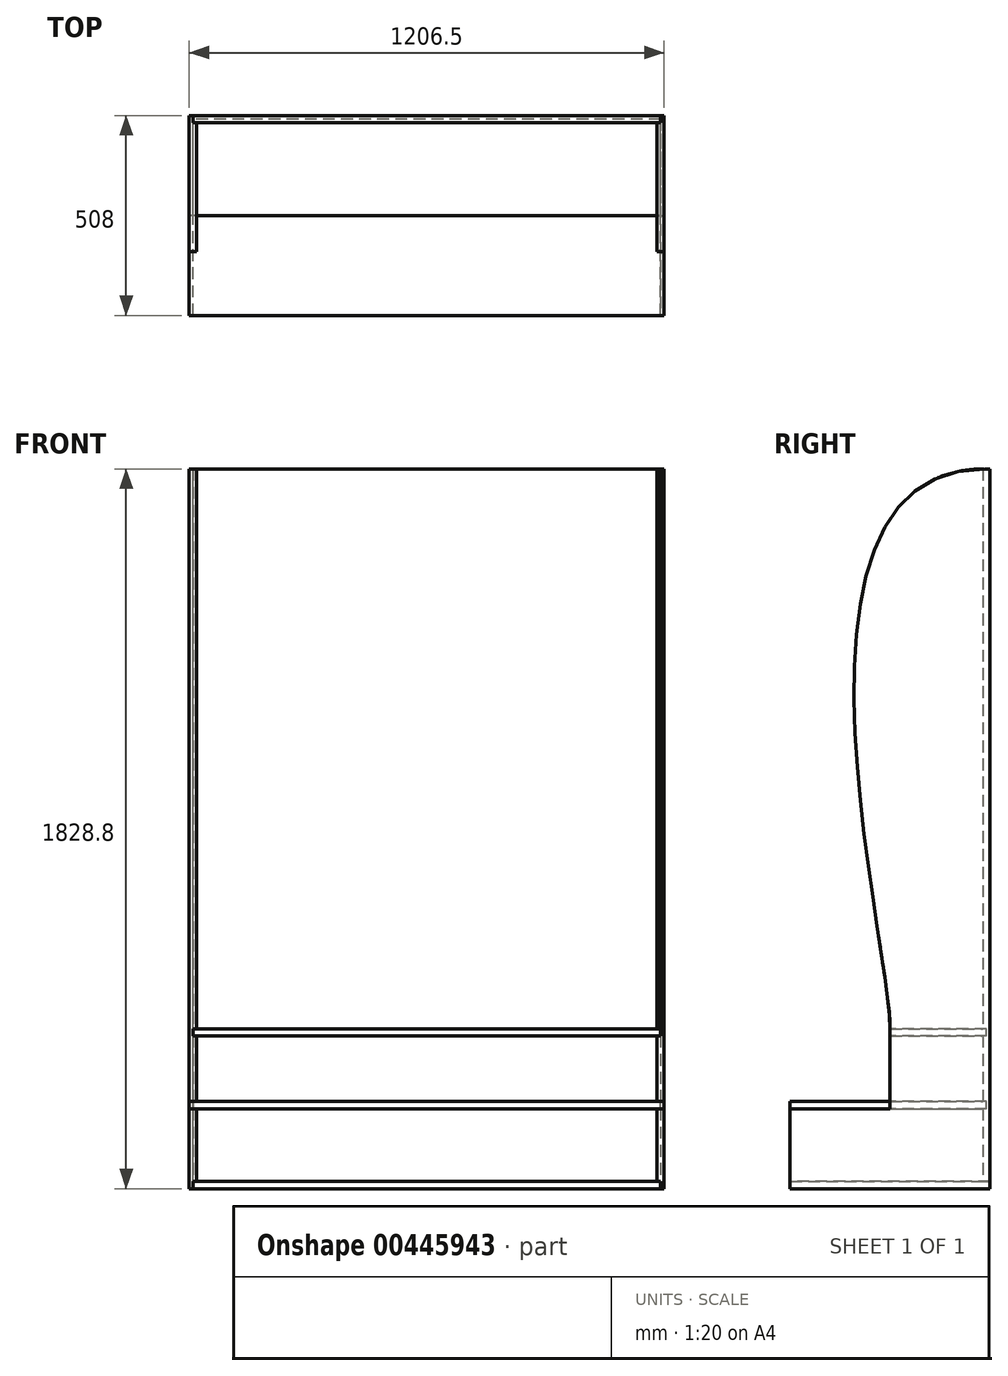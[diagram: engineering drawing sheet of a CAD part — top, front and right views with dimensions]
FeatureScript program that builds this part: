
annotation { "Feature Type Name" : "Feature", "Feature Type Description" : "" }
export const myFeature = defineFeature(function(context is Context, id is Id, definition is map)
    precondition{}
    {
        {
            var Q0;
            Q0=qCreatedBy(makeId("Right.planeOp"),FACE);
            var sketch = newSketch(context, id + "F0", { "sketchPlane" : qUnion([Q0])});
            skLineSegment(sketch, "E0.bottom", {"start": v(0, 0) * mm, "end": v(-508, 0) * mm});
            skLineSegment(sketch, "E0.top", {"start": v(0, 1828.8) * mm, "end": v(-12.7, 1828.8) * mm});
            skLineSegment(sketch, "E0.left", {"start": v(0, 0) * mm, "end": v(0, 1828.8) * mm});
            skLineSegment(sketch, "E0.right", {"start": v(-508, 0) * mm, "end": v(-508, 203.2) * mm});
            skLineSegment(sketch, "E1", {"start": v(-508, 203.2) * mm, "end": v(-254, 203.2) * mm});
            skLineSegment(sketch, "E2", {"start": v(-254, 203.2) * mm, "end": v(-254, 406.4) * mm});
            skFitSpline(sketch, "E3", {"points": [v(-12.7, 1828.8) * mm, v(-254, 406.4) * mm], "startDerivative": vector(-1690.87, 0) * mm, "endDerivative": vector(0, -666.64) * mm});
            skPoint(sketch, "E4", {"position": v(-324.19, 935.7) * mm});
            skSolve(sketch);
        }
        {
            var Q0;
            Q0 = qSketchRegion(id + "F0", true);
            extrude(context, id + "F1", {"entities" : qUnion([Q0]), "depth" : 18 * mm});
        }
        {
            var Q0;
            Q0=makeQuery(id+"F1.opExtrude","CAP_FACE",FACE,{"disambiguationData":[OSD([sQuery(id+"F0.wireOp",EDGE,"E0.bottom"),sQuery(id+"F0.wireOp",EDGE,"E0.top"),sQuery(id+"F0.wireOp",EDGE,"E0.left"),sQuery(id+"F0.wireOp",EDGE,"E0.right"),sQuery(id+"F0.wireOp",EDGE,"E1"),sQuery(id+"F0.wireOp",EDGE,"E2"),sQuery(id+"F0.wireOp",EDGE,"E3")])],"isStart":false});
            var sketch = newSketch(context, id + "F2", { "sketchPlane" : qUnion([Q0])});
            skLineSegment(sketch, "E5.bottom", {"start": v(0, 1828.8) * mm, "end": v(-18, 1828.8) * mm});
            skLineSegment(sketch, "E5.top", {"start": v(0, 0) * mm, "end": v(-18, 0) * mm});
            skLineSegment(sketch, "E5.left", {"start": v(0, 1828.8) * mm, "end": v(0, 0) * mm});
            skLineSegment(sketch, "E5.right", {"start": v(-18, 1828.8) * mm, "end": v(-18, 406.4) * mm});
            skLineSegment(sketch, "E6.bottom", {"start": v(-508, 0) * mm, "end": v(-19.05, 0) * mm});
            skLineSegment(sketch, "E6.top", {"start": v(-508, 18) * mm, "end": v(-18, 18) * mm});
            skLineSegment(sketch, "E6.left", {"start": v(-508, 0) * mm, "end": v(-508, 18) * mm});
            skLineSegment(sketch, "E7.bottom", {"start": v(-254, 406.4) * mm, "end": v(-18, 406.4) * mm});
            skLineSegment(sketch, "E7.top", {"start": v(-254, 388.4) * mm, "end": v(-18, 388.4) * mm});
            skLineSegment(sketch, "E7.left", {"start": v(-254, 406.4) * mm, "end": v(-254, 388.4) * mm});
            skLineSegment(sketch, "E8.trimOffspring", {"start": v(-18, 388.4) * mm, "end": v(-18, 221.2) * mm});
            skLineSegment(sketch, "E9.trimOffspring", {"start": v(-18, 185.2) * mm, "end": v(-18, 18) * mm});
            skLineSegment(sketch, "E10", {"start": v(-254, 203.2) * mm, "end": v(-18, 203.2) * mm});
            skLineSegment(sketch, "E11", {"start": v(-254, 221.2) * mm, "end": v(-18, 221.2) * mm});
            skLineSegment(sketch, "E12", {"start": v(-254, 203.2) * mm, "end": v(-254, 221.2) * mm});
            skLineSegment(sketch, "E13.trimOffspring", {"start": v(-18, 203.2) * mm, "end": v(-18, 185.2) * mm});
            skSolve(sketch);
        }
        {
            var Q0;
            {var subQ8=sQuery(id+"F2.wireOp",EDGE,"E5.top");Q0=makeQuery(id+"F2.imprint","IMPRINT",FACE,{"disambiguationData":[TD([[makeQuery(id+"F2.imprint","IMPRINT",EDGE,{"derivedFrom":subQ8}),-1.0]])]});}
            extrude(context, id + "F3", {"entities" : qUnion([Q0]), "operationType" : NewBodyOperationType.REMOVE, "oppositeDirection" : true, "depth" : 9 * mm});
        }
        {
            var Q0;
            Q0=makeQuery(id+"F1.opExtrude","CAP_FACE",FACE,{"disambiguationData":[OSD([sQuery(id+"F0.wireOp",EDGE,"E0.bottom"),sQuery(id+"F0.wireOp",EDGE,"E0.top"),sQuery(id+"F0.wireOp",EDGE,"E0.left"),sQuery(id+"F0.wireOp",EDGE,"E0.right"),sQuery(id+"F0.wireOp",EDGE,"E1"),sQuery(id+"F0.wireOp",EDGE,"E2"),sQuery(id+"F0.wireOp",EDGE,"E3")])],"isStart":true});
            cPlane(context, id + "F4", {"entities" : qUnion([Q0]), "cplaneType" : CPlaneType.OFFSET, "offset" : 603.25 * mm, "oppositeDirection" : true, "width" : 152.4 * mm, "height" : 152.4 * mm});
        }
        {
            var Q0;
            Q0=makeQuery(id+"F1.opExtrude","SWEPT_BODY",BODY,{"disambiguationData":[OSD([sQuery(id+"F0.wireOp",EDGE,"E0.bottom"),sQuery(id+"F0.wireOp",EDGE,"E0.top"),sQuery(id+"F0.wireOp",EDGE,"E0.left"),sQuery(id+"F0.wireOp",EDGE,"E0.right"),sQuery(id+"F0.wireOp",EDGE,"E1"),sQuery(id+"F0.wireOp",EDGE,"E2"),sQuery(id+"F0.wireOp",EDGE,"E3")])]});
            var Q1;
            Q1=qCreatedBy(id+"F4.planeOp",FACE);
            mirror(context, id + "F5", {"entities" : qUnion([Q0]), "mirrorPlane" : qUnion([Q1])});
        }
        {
            var Q0;
            Q0=makeQuery(id+"F3.boolean.opBoolean","COPY",FACE,{"derivedFrom":makeQuery(id+"F3.opExtrude","CAP_FACE",FACE,{"disambiguationData":[OSD([sQuery(id+"F0.wireOp",EDGE,"E0.bottom"),sQuery(id+"F0.wireOp",EDGE,"E3"),sQuery(id+"F2.wireOp",EDGE,"E5.bottom"),sQuery(id+"F2.wireOp",EDGE,"E5.top"),sQuery(id+"F2.wireOp",EDGE,"E5.left"),sQuery(id+"F2.wireOp",EDGE,"E5.right"),sQuery(id+"F2.wireOp",EDGE,"E6.bottom"),sQuery(id+"F2.wireOp",EDGE,"E6.top"),sQuery(id+"F2.wireOp",EDGE,"E6.left"),sQuery(id+"F2.wireOp",EDGE,"E7.bottom"),sQuery(id+"F2.wireOp",EDGE,"E7.top"),sQuery(id+"F2.wireOp",EDGE,"E7.left"),sQuery(id+"F2.wireOp",EDGE,"E8.trimOffspring"),sQuery(id+"F2.wireOp",EDGE,"E9.trimOffspring"),sQuery(id+"F2.wireOp",EDGE,"E10"),sQuery(id+"F2.wireOp",EDGE,"E11"),sQuery(id+"F2.wireOp",EDGE,"E12"),sQuery(id+"F2.wireOp",EDGE,"E13.trimOffspring")])],"isStart":false})});
            var sketch = newSketch(context, id + "F6", { "sketchPlane" : qUnion([Q0])});
            skLineSegment(sketch, "E14.bottom", {"start": v(-508, 0) * mm, "end": v(0, 0) * mm});
            skLineSegment(sketch, "E14.top", {"start": v(-508, 18) * mm, "end": v(0, 18) * mm});
            skLineSegment(sketch, "E14.left", {"start": v(-508, 0) * mm, "end": v(-508, 18) * mm});
            skLineSegment(sketch, "E14.right", {"start": v(0, 0) * mm, "end": v(0, 18) * mm});
            skSolve(sketch);
        }
        {
            var Q0;
            Q0 = qSketchRegion(id + "F6", true);
            extrude(context, id + "F7", {"entities" : qUnion([Q0]), "endBound" : BoundingType.UP_TO_NEXT, "depth" : 25.4 * mm});
        }
        {
            var Q0;
            Q0=makeQuery(id+"F3.boolean.opBoolean","COPY",FACE,{"derivedFrom":makeQuery(id+"F3.opExtrude","CAP_FACE",FACE,{"disambiguationData":[OSD([sQuery(id+"F0.wireOp",EDGE,"E0.bottom"),sQuery(id+"F0.wireOp",EDGE,"E3"),sQuery(id+"F2.wireOp",EDGE,"E5.bottom"),sQuery(id+"F2.wireOp",EDGE,"E5.top"),sQuery(id+"F2.wireOp",EDGE,"E5.left"),sQuery(id+"F2.wireOp",EDGE,"E5.right"),sQuery(id+"F2.wireOp",EDGE,"E6.bottom"),sQuery(id+"F2.wireOp",EDGE,"E6.top"),sQuery(id+"F2.wireOp",EDGE,"E6.left"),sQuery(id+"F2.wireOp",EDGE,"E7.bottom"),sQuery(id+"F2.wireOp",EDGE,"E7.top"),sQuery(id+"F2.wireOp",EDGE,"E7.left"),sQuery(id+"F2.wireOp",EDGE,"E8.trimOffspring"),sQuery(id+"F2.wireOp",EDGE,"E9.trimOffspring"),sQuery(id+"F2.wireOp",EDGE,"E10"),sQuery(id+"F2.wireOp",EDGE,"E11"),sQuery(id+"F2.wireOp",EDGE,"E12"),sQuery(id+"F2.wireOp",EDGE,"E13.trimOffspring")])],"isStart":false})});
            var sketch = newSketch(context, id + "F8", { "sketchPlane" : qUnion([Q0])});
            skLineSegment(sketch, "E15.bottom", {"start": v(0, 1828.8) * mm, "end": v(-18, 1828.8) * mm});
            skLineSegment(sketch, "E15.top", {"start": v(0, 18) * mm, "end": v(-18, 18) * mm});
            skLineSegment(sketch, "E15.left", {"start": v(0, 1828.8) * mm, "end": v(0, 18) * mm});
            skLineSegment(sketch, "E15.right", {"start": v(-18, 1828.8) * mm, "end": v(-18, 18) * mm});
            skSolve(sketch);
        }
        {
            var Q0;
            {var subQ4=sQuery(id+"F8.wireOp",EDGE,"E15.top");Q0=makeQuery(id+"F8.imprint","IMPRINT",FACE,{"disambiguationData":[TD([[makeQuery(id+"F8.imprint","IMPRINT",EDGE,{"derivedFrom":subQ4}),-1.0]])]});}
            extrude(context, id + "F9", {"entities" : qUnion([Q0]), "endBound" : BoundingType.UP_TO_NEXT, "depth" : 25.4 * mm});
        }
        {
            var Q0;
            Q0=makeQuery(id+"F3.boolean.opBoolean","COPY",FACE,{"derivedFrom":makeQuery(id+"F3.opExtrude","CAP_FACE",FACE,{"disambiguationData":[OSD([sQuery(id+"F0.wireOp",EDGE,"E0.bottom"),sQuery(id+"F0.wireOp",EDGE,"E3"),sQuery(id+"F2.wireOp",EDGE,"E5.bottom"),sQuery(id+"F2.wireOp",EDGE,"E5.top"),sQuery(id+"F2.wireOp",EDGE,"E5.left"),sQuery(id+"F2.wireOp",EDGE,"E5.right"),sQuery(id+"F2.wireOp",EDGE,"E6.bottom"),sQuery(id+"F2.wireOp",EDGE,"E6.top"),sQuery(id+"F2.wireOp",EDGE,"E6.left"),sQuery(id+"F2.wireOp",EDGE,"E7.bottom"),sQuery(id+"F2.wireOp",EDGE,"E7.top"),sQuery(id+"F2.wireOp",EDGE,"E7.left"),sQuery(id+"F2.wireOp",EDGE,"E8.trimOffspring"),sQuery(id+"F2.wireOp",EDGE,"E9.trimOffspring"),sQuery(id+"F2.wireOp",EDGE,"E10"),sQuery(id+"F2.wireOp",EDGE,"E11"),sQuery(id+"F2.wireOp",EDGE,"E12"),sQuery(id+"F2.wireOp",EDGE,"E13.trimOffspring")])],"isStart":false})});
            var sketch = newSketch(context, id + "F10", { "sketchPlane" : qUnion([Q0])});
            skLineSegment(sketch, "E16.bottom", {"start": v(-254, 388.4) * mm, "end": v(-18, 388.4) * mm});
            skLineSegment(sketch, "E16.top", {"start": v(-254, 406.4) * mm, "end": v(-18, 406.4) * mm});
            skLineSegment(sketch, "E16.left", {"start": v(-254, 388.4) * mm, "end": v(-254, 406.4) * mm});
            skLineSegment(sketch, "E17.bottom", {"start": v(-18, 406.4) * mm, "end": v(-9, 406.4) * mm});
            skLineSegment(sketch, "E17.top", {"start": v(-18, 388.4) * mm, "end": v(-9, 388.4) * mm});
            skLineSegment(sketch, "E17.right", {"start": v(-9, 406.4) * mm, "end": v(-9, 388.4) * mm});
            skSolve(sketch);
        }
        {
            var Q0;
            Q0 = qSketchRegion(id + "F10", true);
            extrude(context, id + "F11", {"entities" : qUnion([Q0]), "endBound" : BoundingType.UP_TO_NEXT, "depth" : 25.4 * mm});
        }
        {
            var Q0;
            Q0=makeQuery(id+"F3.boolean.opBoolean","COPY",FACE,{"derivedFrom":makeQuery(id+"F3.opExtrude","CAP_FACE",FACE,{"disambiguationData":[OSD([sQuery(id+"F0.wireOp",EDGE,"E0.bottom"),sQuery(id+"F0.wireOp",EDGE,"E3"),sQuery(id+"F2.wireOp",EDGE,"E5.bottom"),sQuery(id+"F2.wireOp",EDGE,"E5.top"),sQuery(id+"F2.wireOp",EDGE,"E5.left"),sQuery(id+"F2.wireOp",EDGE,"E5.right"),sQuery(id+"F2.wireOp",EDGE,"E6.bottom"),sQuery(id+"F2.wireOp",EDGE,"E6.top"),sQuery(id+"F2.wireOp",EDGE,"E6.left"),sQuery(id+"F2.wireOp",EDGE,"E7.bottom"),sQuery(id+"F2.wireOp",EDGE,"E7.top"),sQuery(id+"F2.wireOp",EDGE,"E7.left"),sQuery(id+"F2.wireOp",EDGE,"E8.trimOffspring"),sQuery(id+"F2.wireOp",EDGE,"E9.trimOffspring"),sQuery(id+"F2.wireOp",EDGE,"E10"),sQuery(id+"F2.wireOp",EDGE,"E11"),sQuery(id+"F2.wireOp",EDGE,"E12"),sQuery(id+"F2.wireOp",EDGE,"E13.trimOffspring")])],"isStart":false})});
            var sketch = newSketch(context, id + "F12", { "sketchPlane" : qUnion([Q0])});
            skLineSegment(sketch, "E18.bottom", {"start": v(-508, 221.2) * mm, "end": v(-18, 221.2) * mm});
            skLineSegment(sketch, "E18.top", {"start": v(-508, 203.2) * mm, "end": v(-18, 203.2) * mm});
            skLineSegment(sketch, "E18.left", {"start": v(-508, 221.2) * mm, "end": v(-508, 203.2) * mm});
            skLineSegment(sketch, "E18.right", {"start": v(-18, 221.2) * mm, "end": v(-18, 203.2) * mm});
            skPoint(sketch, "E19.0", {"position": v(-508, 203.2) * mm});
            skSolve(sketch);
        }
        {
            var Q0;
            Q0=makeQuery(id+"F1.opExtrude","CAP_FACE",FACE,{"disambiguationData":[OSD([sQuery(id+"F0.wireOp",EDGE,"E0.bottom"),sQuery(id+"F0.wireOp",EDGE,"E0.top"),sQuery(id+"F0.wireOp",EDGE,"E0.left"),sQuery(id+"F0.wireOp",EDGE,"E0.right"),sQuery(id+"F0.wireOp",EDGE,"E1"),sQuery(id+"F0.wireOp",EDGE,"E2"),sQuery(id+"F0.wireOp",EDGE,"E3")])],"isStart":true});
            var sketch = newSketch(context, id + "F13", { "sketchPlane" : qUnion([Q0])});
            skLineSegment(sketch, "E20.0", {"start": v(508, 221.2) * mm, "end": v(18, 221.2) * mm});
            skLineSegment(sketch, "E20.1", {"start": v(508, 221.2) * mm, "end": v(508, 203.2) * mm});
            skLineSegment(sketch, "E20.2", {"start": v(508, 203.2) * mm, "end": v(18, 203.2) * mm});
            skLineSegment(sketch, "E21.bottom", {"start": v(18, 221.2) * mm, "end": v(9, 221.2) * mm});
            skLineSegment(sketch, "E21.top", {"start": v(18, 203.2) * mm, "end": v(9, 203.2) * mm});
            skLineSegment(sketch, "E21.right", {"start": v(9, 221.2) * mm, "end": v(9, 203.2) * mm});
            skPoint(sketch, "E20.3.start.orphan", {"position": v(18, 221.2) * mm});
            skSolve(sketch);
        }
        {
            var Q0;
            Q0 = qSketchRegion(id + "F13", true);
            var Q1;
            Q1=makeQuery(id+"F5.opPattern","COPY",FACE,{"derivedFrom":makeQuery(id+"F1.opExtrude","CAP_FACE",FACE,{"disambiguationData":[OSD([sQuery(id+"F0.wireOp",EDGE,"E0.bottom"),sQuery(id+"F0.wireOp",EDGE,"E0.top"),sQuery(id+"F0.wireOp",EDGE,"E0.left"),sQuery(id+"F0.wireOp",EDGE,"E0.right"),sQuery(id+"F0.wireOp",EDGE,"E1"),sQuery(id+"F0.wireOp",EDGE,"E2"),sQuery(id+"F0.wireOp",EDGE,"E3")])],"isStart":true}),"instanceName":"1"});
            extrude(context, id + "F14", {"entities" : qUnion([Q0]), "endBound" : BoundingType.UP_TO_SURFACE, "oppositeDirection" : true, "endBoundEntityFace" : qUnion([Q1]), "depth" : 25.4 * mm});
        }
        {
            var Q0;
            Q0=makeQuery(id+"F1.opExtrude","SWEPT_BODY",BODY,{"disambiguationData":[OSD([sQuery(id+"F0.wireOp",EDGE,"E0.bottom"),sQuery(id+"F0.wireOp",EDGE,"E0.top"),sQuery(id+"F0.wireOp",EDGE,"E0.left"),sQuery(id+"F0.wireOp",EDGE,"E0.right"),sQuery(id+"F0.wireOp",EDGE,"E1"),sQuery(id+"F0.wireOp",EDGE,"E2"),sQuery(id+"F0.wireOp",EDGE,"E3")])]});
            var Q1;
            Q1=makeQuery(id+"F5.opPattern","COPY",BODY,{"derivedFrom":makeQuery(id+"F1.opExtrude","SWEPT_BODY",BODY,{"disambiguationData":[OSD([sQuery(id+"F0.wireOp",EDGE,"E0.bottom"),sQuery(id+"F0.wireOp",EDGE,"E0.top"),sQuery(id+"F0.wireOp",EDGE,"E0.left"),sQuery(id+"F0.wireOp",EDGE,"E0.right"),sQuery(id+"F0.wireOp",EDGE,"E1"),sQuery(id+"F0.wireOp",EDGE,"E2"),sQuery(id+"F0.wireOp",EDGE,"E3")])]}),"instanceName":"1"});
            var Q2;
            Q2=makeQuery(id+"F14.opExtrude","SWEPT_BODY",BODY,{"disambiguationData":[OSD([sQuery(id+"F13.wireOp",EDGE,"E20.0"),sQuery(id+"F13.wireOp",EDGE,"E20.1"),sQuery(id+"F13.wireOp",EDGE,"E20.2"),sQuery(id+"F13.wireOp",EDGE,"E20.3")])]});
            booleanBodies(context, id + "F15", {"operationType" : BooleanOperationType.SUBTRACTION, "tools" : qUnion([Q0, Q1]), "targets" : qUnion([Q2]), "keepTools" : true});
        }
        {
            var Q0;
            Q0=makeQuery(id+"F11.opExtrude","SWEPT_BODY",BODY,{"disambiguationData":[OSD([sQuery(id+"F10.wireOp",EDGE,"E16.bottom"),sQuery(id+"F10.wireOp",EDGE,"E16.top"),sQuery(id+"F10.wireOp",EDGE,"E16.left"),sQuery(id+"F10.wireOp",EDGE,"E17.bottom"),sQuery(id+"F10.wireOp",EDGE,"E17.top"),sQuery(id+"F10.wireOp",EDGE,"E17.right")])]});
            var Q1;
            Q1=makeQuery(id+"F14.opExtrude","SWEPT_BODY",BODY,{"disambiguationData":[OSD([sQuery(id+"F13.wireOp",EDGE,"E20.0"),sQuery(id+"F13.wireOp",EDGE,"E20.1"),sQuery(id+"F13.wireOp",EDGE,"E20.2"),sQuery(id+"F13.wireOp",EDGE,"E21.bottom"),sQuery(id+"F13.wireOp",EDGE,"E21.top"),sQuery(id+"F13.wireOp",EDGE,"E21.right")])]});
            var Q2;
            Q2=makeQuery(id+"F9.opExtrude","SWEPT_BODY",BODY,{"disambiguationData":[OSD([sQuery(id+"F0.wireOp",EDGE,"E3"),sQuery(id+"F8.wireOp",EDGE,"E15.bottom"),sQuery(id+"F8.wireOp",EDGE,"E15.top"),sQuery(id+"F8.wireOp",EDGE,"E15.left"),sQuery(id+"F8.wireOp",EDGE,"E15.right")])]});
            booleanBodies(context, id + "F16", {"operationType" : BooleanOperationType.SUBTRACTION, "tools" : qUnion([Q0, Q1]), "targets" : qUnion([Q2]), "keepTools" : true});
        }
    });
